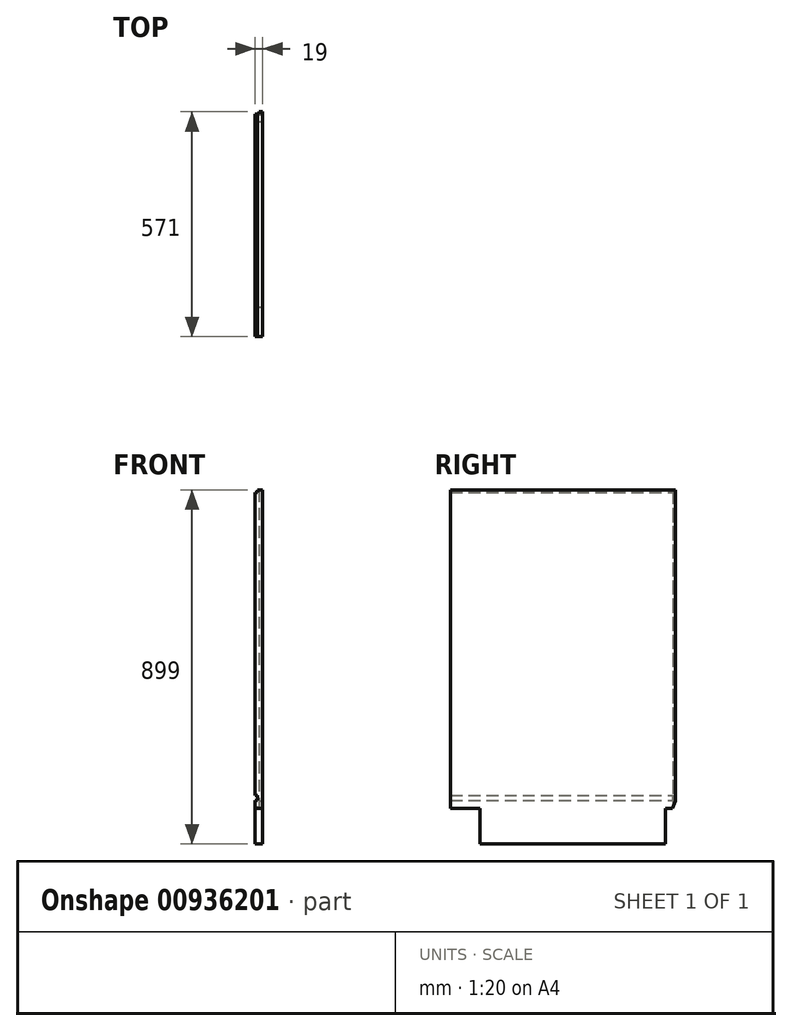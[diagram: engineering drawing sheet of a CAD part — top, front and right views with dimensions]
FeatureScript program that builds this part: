
annotation { "Feature Type Name" : "Feature", "Feature Type Description" : "" }
export const myFeature = defineFeature(function(context is Context, id is Id, definition is map)
    precondition{}
    {
        {
            var Q0;
            Q0=qCreatedBy(makeId("Right.planeOp"),FACE);
            var sketch = newSketch(context, id + "F0", { "sketchPlane" : qUnion([Q0])});
            skLineSegment(sketch, "E0.bottom", {"start": v(0, 0) * mm, "end": v(-496, 0) * mm});
            skLineSegment(sketch, "E0.top", {"start": v(0, 899) * mm, "end": v(-571, 899) * mm});
            skLineSegment(sketch, "E0.left", {"start": v(0, 0) * mm, "end": v(0, 899) * mm});
            skLineSegment(sketch, "E0.right", {"start": v(-571, 90) * mm, "end": v(-571, 899) * mm});
            skLineSegment(sketch, "E1", {"start": v(-571, 90) * mm, "end": v(-496, 90) * mm});
            skLineSegment(sketch, "E2", {"start": v(-496, 90) * mm, "end": v(-496, 0) * mm});
            skSolve(sketch);
        }
        {
            var Q0;
            Q0=makeQuery(id+"F0.imprint","IMPRINT",FACE,{"disambiguationData":[TD([[makeQuery(id+"F0.imprint","IMPRINT",EDGE,{"derivedFrom":sQuery(id+"F0.wireOp",EDGE,"E0.bottom")}),-1.0]])]});
            extrude(context, id + "F1", {"entities" : qUnion([Q0]), "oppositeDirection" : true, "depth" : 19 * mm, "offsetDistance" : 25 * mm});
        }
        {
            var Q0;
            Q0=qCreatedBy(makeId("Front.planeOp"),FACE);
            var sketch = newSketch(context, id + "F2", { "sketchPlane" : qUnion([Q0])});
            skLineSegment(sketch, "E3.0", {"start": v(-19, 0) * mm, "end": v(-19, 899) * mm, "construction": true});
            skLineSegment(sketch, "E4.bottom", {"start": v(-19, 110) * mm, "end": v(-13, 110) * mm});
            skLineSegment(sketch, "E4.top", {"start": v(-19, 122.5) * mm, "end": v(-13, 122.5) * mm});
            skLineSegment(sketch, "E4.left", {"start": v(-19, 110) * mm, "end": v(-19, 122.5) * mm});
            skLineSegment(sketch, "E4.right", {"start": v(-13, 110) * mm, "end": v(-13, 122.5) * mm});
            skSolve(sketch);
        }
        {
            var Q0;
            Q0 = qSketchRegion(id + "F2", true);
            extrude(context, id + "F3", {"entities" : qUnion([Q0]), "operationType" : NewBodyOperationType.REMOVE, "endBound" : BoundingType.THROUGH_ALL, "depth" : 25 * mm, "offsetDistance" : 25 * mm});
        }
        {
            var Q0;
            Q0=qCreatedBy(makeId("Top.planeOp"),FACE);
            var sketch = newSketch(context, id + "F4", { "sketchPlane" : qUnion([Q0])});
            skLineSegment(sketch, "E5.bottom", {"start": v(-9.5, 0) * mm, "end": v(-19, 0) * mm});
            skLineSegment(sketch, "E5.top", {"start": v(-9.5, -6) * mm, "end": v(-19, -6) * mm});
            skLineSegment(sketch, "E5.left", {"start": v(-9.5, 0) * mm, "end": v(-9.5, -6) * mm});
            skLineSegment(sketch, "E5.right", {"start": v(-19, 0) * mm, "end": v(-19, -6) * mm});
            skSolve(sketch);
        }
        {
            var Q0;
            Q0 = qSketchRegion(id + "F4", true);
            extrude(context, id + "F5", {"entities" : qUnion([Q0]), "operationType" : NewBodyOperationType.REMOVE, "endBound" : BoundingType.THROUGH_ALL, "depth" : 25 * mm, "offsetDistance" : 25 * mm});
        }
        {
            var Q0;
            Q0=qCreatedBy(makeId("Right.planeOp"),FACE);
            var sketch = newSketch(context, id + "F6", { "sketchPlane" : qUnion([Q0])});
            skLineSegment(sketch, "E6.bottom", {"start": v(0, 0) * mm, "end": v(-25, 0) * mm});
            skLineSegment(sketch, "E6.top", {"start": v(0, 90) * mm, "end": v(-25, 90) * mm, "construction": true});
            skLineSegment(sketch, "E6.left", {"start": v(0, 0) * mm, "end": v(0, 109) * mm});
            skLineSegment(sketch, "E6.right", {"start": v(-25, 0) * mm, "end": v(-25, 90) * mm});
            skLineSegment(sketch, "E7", {"start": v(0, 109) * mm, "end": v(-6.92, 90) * mm});
            skLineSegment(sketch, "E8", {"start": v(-6.92, 90) * mm, "end": v(-25, 90) * mm});
            skSolve(sketch);
        }
        {
            var Q0;
            Q0 = qSketchRegion(id + "F6", true);
            extrude(context, id + "F7", {"entities" : qUnion([Q0]), "operationType" : NewBodyOperationType.REMOVE, "endBound" : BoundingType.THROUGH_ALL, "oppositeDirection" : true, "depth" : 25 * mm, "offsetDistance" : 25 * mm});
        }
        {
            var Q0;
            Q0=qCreatedBy(makeId("Front.planeOp"),FACE);
            var sketch = newSketch(context, id + "F8", { "sketchPlane" : qUnion([Q0])});
            skLineSegment(sketch, "E9.1", {"start": v(-19, 899) * mm, "end": v(0, 899) * mm, "construction": true});
            skLineSegment(sketch, "E10.bottom", {"start": v(-19, 899) * mm, "end": v(-13, 899) * mm});
            skLineSegment(sketch, "E10.top", {"start": v(-19, 893) * mm, "end": v(-13, 893) * mm});
            skLineSegment(sketch, "E10.left", {"start": v(-19, 899) * mm, "end": v(-19, 893) * mm});
            skLineSegment(sketch, "E10.right", {"start": v(-13, 899) * mm, "end": v(-13, 893) * mm});
            skSolve(sketch);
        }
        {
            var Q0;
            Q0 = qSketchRegion(id + "F8", true);
            extrude(context, id + "F9", {"entities" : qUnion([Q0]), "operationType" : NewBodyOperationType.REMOVE, "endBound" : BoundingType.THROUGH_ALL, "depth" : 25 * mm, "offsetDistance" : 25 * mm});
        }
    });
